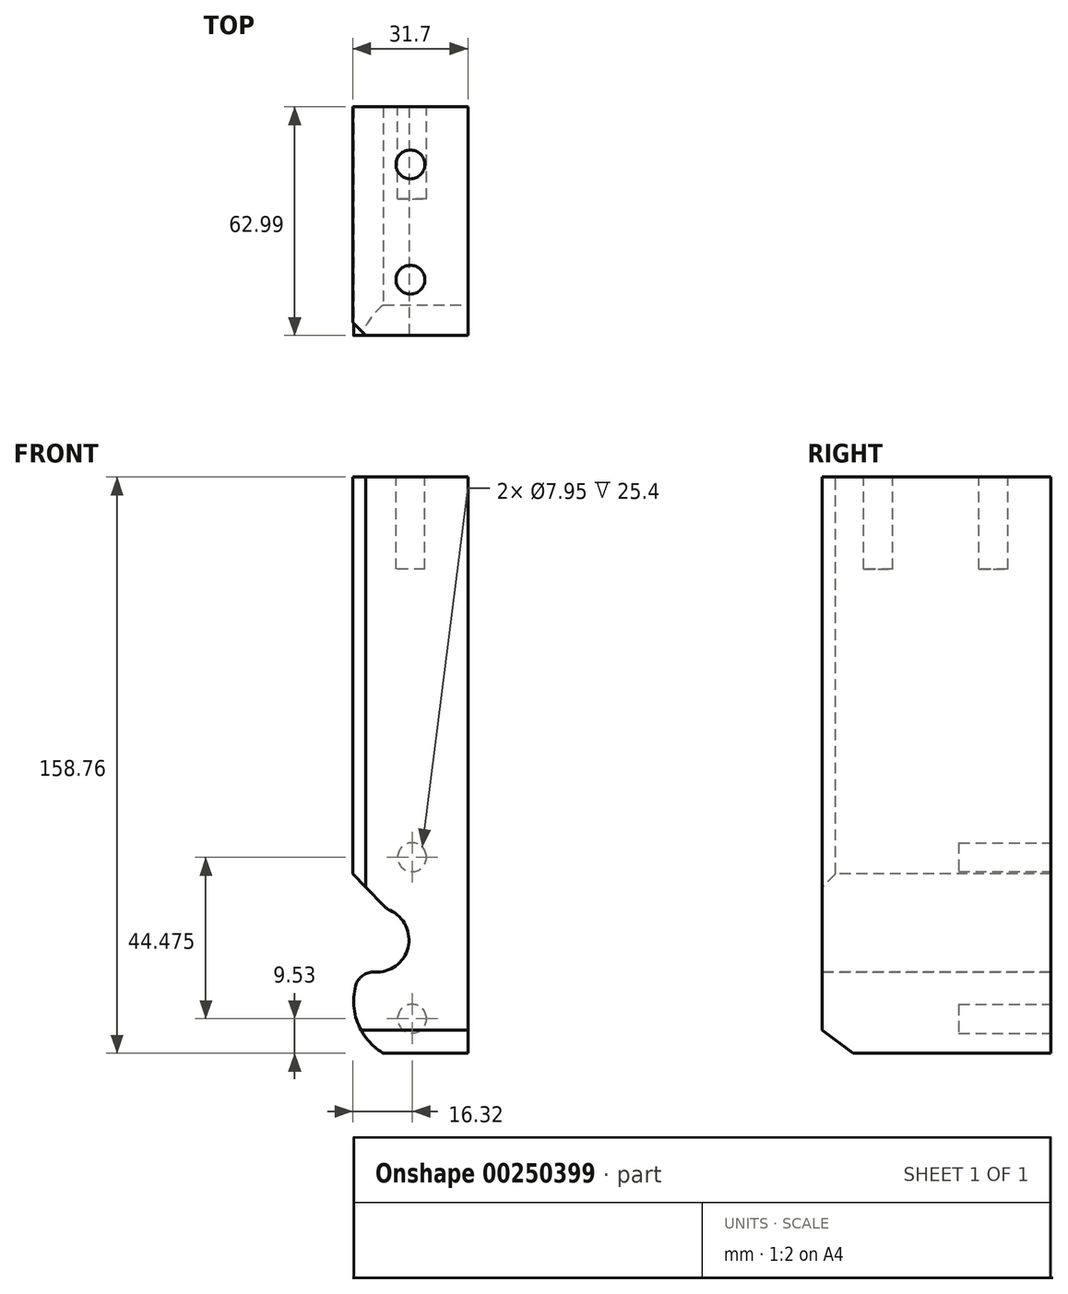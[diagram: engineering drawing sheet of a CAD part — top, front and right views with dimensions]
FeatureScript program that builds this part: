
annotation { "Feature Type Name" : "Feature", "Feature Type Description" : "" }
export const myFeature = defineFeature(function(context is Context, id is Id, definition is map)
    precondition{}
    {
        {
            var Q0;
            Q0=qCreatedBy(makeId("Front.planeOp"),FACE);
            var sketch = newSketch(context, id + "F0", { "sketchPlane" : qUnion([Q0])});
            skLineSegment(sketch, "E0.bottom", {"start": v(15.85, -79.38) * mm, "end": v(-15.85, -79.38) * mm});
            skLineSegment(sketch, "E0.top", {"start": v(15.85, 79.38) * mm, "end": v(-15.85, 79.38) * mm});
            skLineSegment(sketch, "E0.left", {"start": v(15.85, -79.38) * mm, "end": v(15.85, 79.38) * mm});
            skLineSegment(sketch, "E0.right", {"start": v(-15.85, -79.38) * mm, "end": v(-15.85, 79.38) * mm});
            skPoint(sketch, "E0.middle", {"position": v(0, 0) * mm});
            skSolve(sketch);
        }
        {
            var Q0;
            Q0=makeQuery(id+"F0.imprint","IMPRINT",FACE,{"disambiguationData":[TD([[makeQuery(id+"F0.imprint","IMPRINT",EDGE,{"derivedFrom":sQuery(id+"F0.wireOp",EDGE,"E0.bottom")}),-1.0]])]});
            extrude(context, id + "F1", {"entities" : qUnion([Q0]), "depth" : 63 * mm});
        }
        {
            var Q0;
            Q0=makeQuery(id+"F1.opExtrude","CAP_FACE",FACE,{"disambiguationData":[OSD([sQuery(id+"F0.wireOp",EDGE,"E0.bottom"),sQuery(id+"F0.wireOp",EDGE,"E0.top"),sQuery(id+"F0.wireOp",EDGE,"E0.left"),sQuery(id+"F0.wireOp",EDGE,"E0.right")])],"isStart":false});
            var sketch = newSketch(context, id + "F2", { "sketchPlane" : qUnion([Q0])});
            skLineSegment(sketch, "E1", {"start": v(-15.85, 79.38) * mm, "end": v(-15.85, -29.9) * mm});
            skLineSegment(sketch, "E2", {"start": v(-15.85, -29.9) * mm, "end": v(-6.4, -39.69) * mm});
            skLineSegment(sketch, "E3", {"start": v(0, -48.1) * mm, "end": v(-0.4, -48.1) * mm});
            skArc(sketch, "E4", {"start": v(-13.1, -56.18) * mm, "mid": v(-1.06, -51.47) * mm, "end": v(-6.4, -39.69) * mm});
            skPoint(sketch, "E5.start.orphan", {"position": v(0, 79.38) * mm});
            skLineSegment(sketch, "E6", {"start": v(0, 79.38) * mm, "end": v(0, -66.95) * mm});
            skLineSegment(sketch, "E7", {"start": v(0, -66.95) * mm, "end": v(-0.28, -66.95) * mm});
            skLineSegment(sketch, "E8", {"start": v(-0.28, -66.95) * mm, "end": v(1.1, -65) * mm});
            skArc(sketch, "E9", {"start": v(0, -48.32) * mm, "mid": v(-0.2, -48.34) * mm, "end": v(-0.4, -48.35) * mm});
            skLineSegment(sketch, "E10", {"start": v(-15.85, -79.38) * mm, "end": v(15.85, -79.38) * mm});
            skArc(sketch, "E11.trimOffspring", {"start": v(-13.1, -56.18) * mm, "mid": v(-15.14, -68.97) * mm, "end": v(-7.43, -79.38) * mm});
            skSolve(sketch);
        }
        {
            var Q0;
            {var subQ1=sQuery(id+"F2.wireOp",EDGE,"E2");Q0=makeQuery(id+"F2.imprint","IMPRINT",FACE,{"disambiguationData":[TD([[makeQuery(id+"F2.imprint","IMPRINT",EDGE,{"derivedFrom":subQ1}),-1.0]])]});}
            extrude(context, id + "F3", {"entities" : qUnion([Q0]), "operationType" : NewBodyOperationType.REMOVE, "endBound" : BoundingType.THROUGH_ALL, "oppositeDirection" : true, "depth" : 25.4 * mm});
        }
        {
            var Q0;
            Q0=makeQuery(id+"F1.opExtrude","SWEPT_FACE",FACE,{"disambiguationData":[OSD([sQuery(id+"F0.wireOp",EDGE,"E0.top")])]});
            var sketch = newSketch(context, id + "F4", { "sketchPlane" : qUnion([Q0])});
            skCircle(sketch, "E12", {"center": v(0, -15.88) * mm, "radius": 3.98 * mm});
            skCircle(sketch, "E13", {"center": v(0, -47.62) * mm, "radius": 3.98 * mm});
            skSolve(sketch);
        }
        {
            var Q0;
            Q0=makeQuery(id+"F4.imprint","IMPRINT",FACE,{"disambiguationData":[TD([[makeQuery(id+"F4.imprint","IMPRINT",EDGE,{"derivedFrom":sQuery(id+"F4.wireOp",EDGE,"E12")}),1.0]])]});
            var Q1;
            Q1=makeQuery(id+"F4.imprint","IMPRINT",FACE,{"disambiguationData":[TD([[makeQuery(id+"F4.imprint","IMPRINT",EDGE,{"derivedFrom":sQuery(id+"F4.wireOp",EDGE,"E13")}),1.0]])]});
            extrude(context, id + "F5", {"entities" : qUnion([Q0, Q1]), "operationType" : NewBodyOperationType.REMOVE, "oppositeDirection" : true, "depth" : 25.4 * mm});
        }
        {
            var Q0;
            Q0=makeQuery(id+"F1.opExtrude","CAP_FACE",FACE,{"disambiguationData":[OSD([sQuery(id+"F0.wireOp",EDGE,"E0.bottom"),sQuery(id+"F0.wireOp",EDGE,"E0.top"),sQuery(id+"F0.wireOp",EDGE,"E0.left"),sQuery(id+"F0.wireOp",EDGE,"E0.right")])],"isStart":true});
            var sketch = newSketch(context, id + "F6", { "sketchPlane" : qUnion([Q0])});
            skCircle(sketch, "E14", {"center": v(-0.47, -69.85) * mm, "radius": 3.98 * mm});
            skLineSegment(sketch, "E15", {"start": v(-0.47, -69.85) * mm, "end": v(-0.47, -25.37) * mm});
            skCircle(sketch, "E16", {"center": v(-0.47, -25.37) * mm, "radius": 3.98 * mm});
            skSolve(sketch);
        }
        {
            var Q0;
            Q0=makeQuery(id+"F6.imprint","IMPRINT",FACE,{"disambiguationData":[TD([[makeQuery(id+"F6.imprint","IMPRINT",EDGE,{"derivedFrom":sQuery(id+"F6.wireOp",EDGE,"E16")}),1.0]])]});
            var Q1;
            Q1=makeQuery(id+"F6.imprint","IMPRINT",FACE,{"disambiguationData":[TD([[makeQuery(id+"F6.imprint","IMPRINT",EDGE,{"derivedFrom":sQuery(id+"F6.wireOp",EDGE,"E14")}),1.0]])]});
            extrude(context, id + "F7", {"entities" : qUnion([Q0, Q1]), "operationType" : NewBodyOperationType.REMOVE, "oppositeDirection" : true, "depth" : 25.4 * mm});
        }
        {
            var Q0;
            Q0=makeQuery(id+"F1.opExtrude","SWEPT_FACE",FACE,{"disambiguationData":[OSD([sQuery(id+"F0.wireOp",EDGE,"E0.left")])]});
            var sketch = newSketch(context, id + "F8", { "sketchPlane" : qUnion([Q0])});
            skLineSegment(sketch, "E17", {"start": v(-63, 79.38) * mm, "end": v(-63, -73.02) * mm});
            skLineSegment(sketch, "E18", {"start": v(0, -79.38) * mm, "end": v(-54.56, -79.38) * mm});
            skLineSegment(sketch, "E19", {"start": v(-54.56, -79.38) * mm, "end": v(-63, -73.02) * mm});
            skSolve(sketch);
        }
        {
            var Q0;
            {var subQ0=sQuery(id+"F8.wireOp",EDGE,"E19");Q0=makeQuery(id+"F8.imprint","IMPRINT",FACE,{"disambiguationData":[TD([[makeQuery(id+"F8.imprint","IMPRINT",EDGE,{"derivedFrom":subQ0}),1.0]])]});}
            extrude(context, id + "F9", {"entities" : qUnion([Q0]), "operationType" : NewBodyOperationType.REMOVE, "endBound" : BoundingType.THROUGH_ALL, "oppositeDirection" : true, "depth" : 25.4 * mm});
        }
        {
            var Q0;
            Q0=makeQuery(id+"F1.opExtrude","CAP_EDGE",EDGE,{"disambiguationData":[OSD([sQuery(id+"F0.wireOp",EDGE,"E0.right")])],"isStart":false});
            var Q1;
            Q1=makeQuery(id+"F3.boolean.opBoolean","COPY",EDGE,{"derivedFrom":makeQuery(id+"F3.opExtrude","CAP_EDGE",EDGE,{"disambiguationData":[OSD([sQuery(id+"F2.wireOp",EDGE,"E2")])],"isStart":true})});
            var Q2;
            Q2=makeQuery(id+"F3.boolean.opBoolean","COPY",EDGE,{"derivedFrom":makeQuery(id+"F3.opExtrude","CAP_EDGE",EDGE,{"disambiguationData":[OSD([sQuery(id+"F2.wireOp",EDGE,"E4")])],"isStart":true})});
            var Q3;
            Q3=makeQuery(id+"F3.boolean.opBoolean","COPY",EDGE,{"derivedFrom":makeQuery(id+"F3.opExtrude","CAP_EDGE",EDGE,{"disambiguationData":[OSD([sQuery(id+"F2.wireOp",EDGE,"E11.trimOffspring")])],"isStart":true})});
            chamfer(context, id + "F10", {"entities" : qUnion([Q0, Q1, Q2, Q3]), "width" : 3.6 * mm, "tangentPropagation" : true});
        }
        {
            var Q0;
            Q0=makeQuery(id+"F3.boolean.opBoolean","COPY",EDGE,{"derivedFrom":makeQuery(id+"F3.opExtrude","SWEPT_EDGE",EDGE,{"disambiguationData":[OSD([sQuery(id+"F2.wireOp",EDGE,"E4"),sQuery(id+"F2.wireOp",EDGE,"E11.trimOffspring")])]})});
            var Q1;
            Q1=makeQuery(id+"F3.boolean.opBoolean","COPY",EDGE,{"derivedFrom":makeQuery(id+"F3.opExtrude","SWEPT_EDGE",EDGE,{"disambiguationData":[OSD([sQuery(id+"F0.wireOp",EDGE,"E0.right"),sQuery(id+"F2.wireOp",EDGE,"E1"),sQuery(id+"F2.wireOp",EDGE,"E2")])]})});
            var Q2;
            Q2=makeQuery(id+"F3.boolean.opBoolean","COPY",EDGE,{"derivedFrom":makeQuery(id+"F3.opExtrude","SWEPT_EDGE",EDGE,{"disambiguationData":[OSD([sQuery(id+"F2.wireOp",EDGE,"E2"),sQuery(id+"F2.wireOp",EDGE,"E4")])]})});
            var Q3;
            Q3=makeQuery(id+"F10.opChamfer","BLEND_EDGE",EDGE,{"blendedFrom":[makeQuery(id+"F3.boolean.opBoolean","COPY",EDGE,{"derivedFrom":makeQuery(id+"F3.opExtrude","CAP_EDGE",EDGE,{"disambiguationData":[OSD([sQuery(id+"F2.wireOp",EDGE,"E2")])],"isStart":true})}),makeQuery(id+"F1.opExtrude","CAP_EDGE",EDGE,{"disambiguationData":[OSD([sQuery(id+"F0.wireOp",EDGE,"E0.right")])],"isStart":false})],"blendedInto":[]});
            var Q4;
            Q4=makeQuery(id+"F10.opChamfer","BLEND_EDGE",EDGE,{"blendedFrom":[makeQuery(id+"F3.boolean.opBoolean","COPY",EDGE,{"derivedFrom":makeQuery(id+"F3.opExtrude","CAP_EDGE",EDGE,{"disambiguationData":[OSD([sQuery(id+"F2.wireOp",EDGE,"E2")])],"isStart":true})}),makeQuery(id+"F3.boolean.opBoolean","COPY",EDGE,{"derivedFrom":makeQuery(id+"F3.opExtrude","CAP_EDGE",EDGE,{"disambiguationData":[OSD([sQuery(id+"F2.wireOp",EDGE,"E4")])],"isStart":true})})],"blendedInto":[]});
            var Q5;
            Q5=makeQuery(id+"F10.opChamfer","BLEND_EDGE",EDGE,{"blendedFrom":[makeQuery(id+"F3.boolean.opBoolean","COPY",EDGE,{"derivedFrom":makeQuery(id+"F3.opExtrude","CAP_EDGE",EDGE,{"disambiguationData":[OSD([sQuery(id+"F2.wireOp",EDGE,"E4")])],"isStart":true})}),makeQuery(id+"F3.boolean.opBoolean","COPY",EDGE,{"derivedFrom":makeQuery(id+"F3.opExtrude","CAP_EDGE",EDGE,{"disambiguationData":[OSD([sQuery(id+"F2.wireOp",EDGE,"E11.trimOffspring")])],"isStart":true})})],"blendedInto":[]});
            fillet(context, id + "F11", {"entities" : qUnion([Q0, Q1, Q2, Q3, Q4, Q5]), "radius" : 5.08 * mm, "tangentPropagation" : true, "allowEdgeOverflow" : false});
        }
    });
